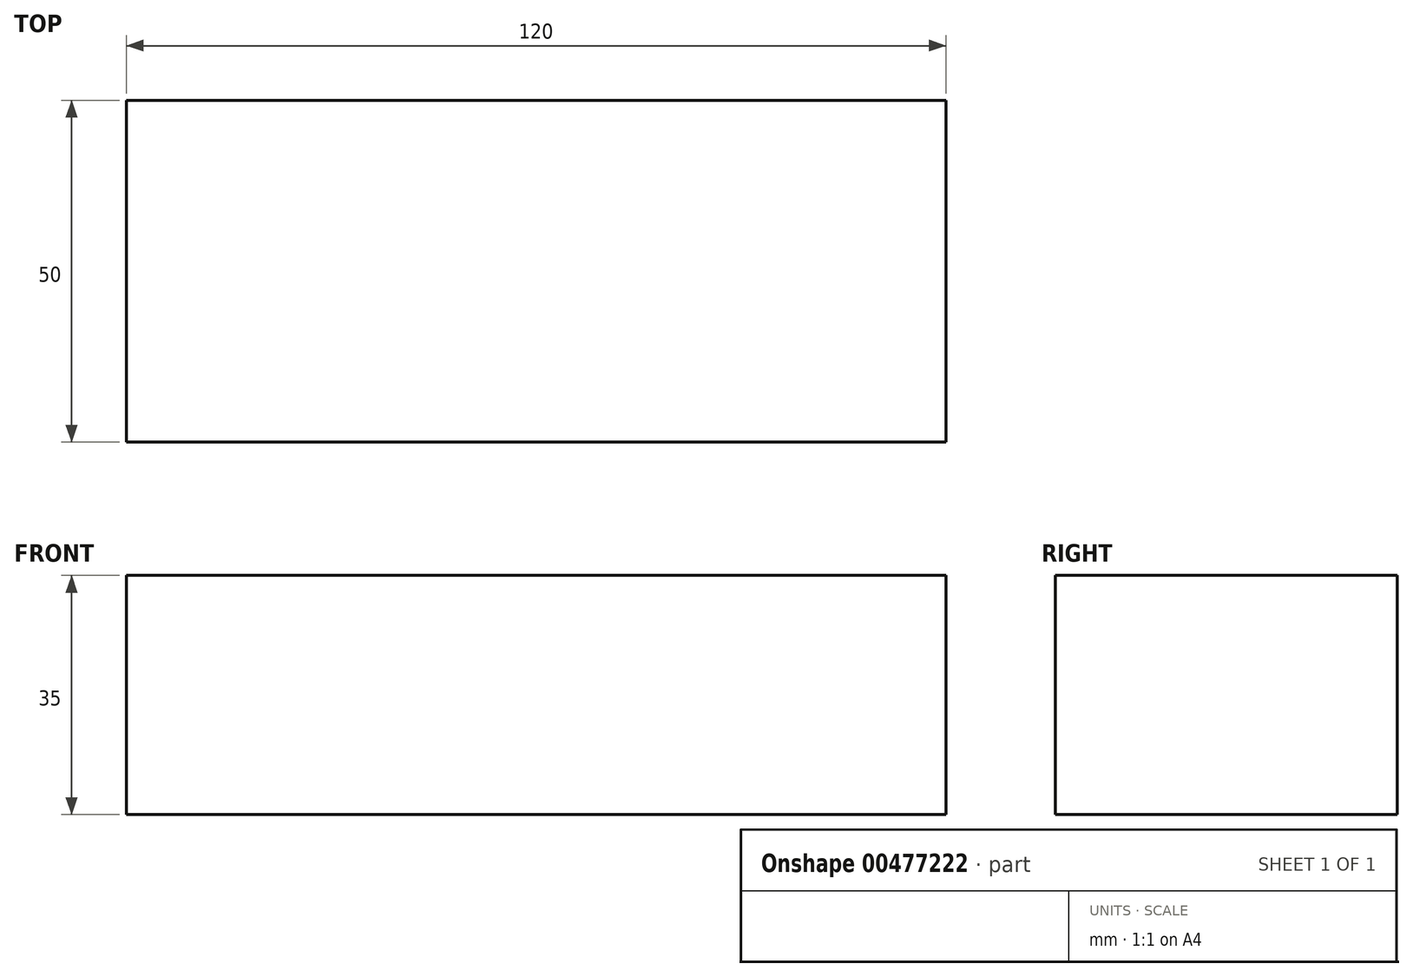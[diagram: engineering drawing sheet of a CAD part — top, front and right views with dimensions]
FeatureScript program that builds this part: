
annotation { "Feature Type Name" : "Feature", "Feature Type Description" : "" }
export const myFeature = defineFeature(function(context is Context, id is Id, definition is map)
    precondition{}
    {
        {
            var Q0;
            Q0=qCreatedBy(makeId("Right.planeOp"),FACE);
            var sketch = newSketch(context, id + "F0", { "sketchPlane" : qUnion([Q0])});
            skLineSegment(sketch, "E0", {"start": v(0, 0) * mm, "end": v(-35, 0) * mm});
            skLineSegment(sketch, "E1.bottom", {"start": v(-35, 0) * mm, "end": v(-85, 0) * mm});
            skLineSegment(sketch, "E1.top", {"start": v(-35, -35) * mm, "end": v(-85, -35) * mm});
            skLineSegment(sketch, "E1.left", {"start": v(-35, 0) * mm, "end": v(-35, -35) * mm});
            skLineSegment(sketch, "E1.right", {"start": v(-85, 0) * mm, "end": v(-85, -35) * mm});
            skSolve(sketch);
        }
        {
            var Q0;
            Q0=qSketchRegion(id+"F0",true);
            extrude(context, id + "F1", {"entities" : qUnion([Q0]), "endBound" : BoundingType.SYMMETRIC, "depth" : 120 * mm});
        }
    });
